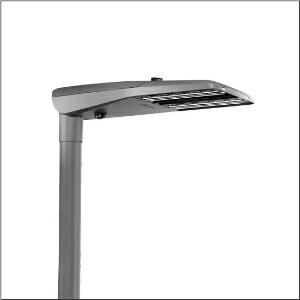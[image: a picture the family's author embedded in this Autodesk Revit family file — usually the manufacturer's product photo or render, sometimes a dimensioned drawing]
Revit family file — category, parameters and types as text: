
# Revit family: streetlight_sl_11_iq_midi___pc-r_5xc3f21y08me_3682
name_source: partatom
category: Lighting Fixtures
units: mm (PartAtom-declared; Revit-internal decimal feet)

## family parameters
Cut with Voids When Loaded = No
Host = Face
Light Source = No
Part Type = Normal
Room Calculation Point = No
Round Connector Dimension = Use Diameter
Shared = No

## types (1)
- --- (1 x LED, 12730 lm, 122.8 W, 2200K)
    Apparent Load = 123 VA
    CIE Flux Codes = 37 73 96 100 100
    Color Rendering = 70
    Color Temperature = 2200K
    Default Elevation = 1800 mm
    Description = Streetlight SL 11 iQ midi, mast luminaire, primary light control with 3 zone facetted reflector, of plastic, silver coated, highly specular, primary optical cover: cover, of PMMA, transparent, light distribution: PC-R, light emission: direct distribution, primary light characteristic: asymmetric, right, installation type: post-top, side-entry, LED, High Power LED, rated luminous flux: 12.730lm, luminous efficacy: 104lm/W, light colour: 722, colour temperature: 2200K, control: presetting dimming logarithmic, Street-Remote, Auto-Match, Temp-Guard, Lumen-Switch, Night-Set, Smart-Wire, Light-Fading, Desk-Remote (wireless, voltage-free reading and setting of iQ features in the workshop via application-optimized NFC function/RFID function), optimised constant luminous flux control (CLO 2.0), with cable H07RN-F 5x 1.5mm², mains connection: 230..240V, AC, 50/60Hz, connection cable pre-assembled, cable length: 12,5m, start of lifetime: 123W, end of service life: 130W, reduction: 56W, luminaire housing, of diecast aluminium, powder-coated, Siteco® metallic grey (DB 702S), please order mast flange separately, inclination adjustable without tools: 0°, 5°, 10°, 15° (post-top) | 0°, -5°, -10°, -15° (side-entry), sealing non-destructively replaceable, multi-level sealing system, length: 780mm, width: 376mm, height: 118mm, mast flange for spigot size: 42mm (side-entry): 5XC10008XM4, 60/48mm (side-entry/post-top): 5XC10108XM2, 76/60mm (side-entry/post-top): 5XC10108XM1, equipment: Power, Smart Interface below and above, protection rating (complete): IP66, insulation class (complete): insulation class II (safety insulation), certification: CE, ENEC, VDE, UKCA, impact resistance: IK09, permissible operating ambient temperature for outdoor applications: -25..+50°C, standard-compliant lighting for roads and squares, Environmental Product Declaration (EPD) tested and certified by an independent institute, packaging unit: 1 piece

Light Distribution: PC-R
    Height = 118 mm
    Lamp = 1 x LED
    Lamp Light Flux = 12730 lm
    Lamp Power = 122.8 W
    Lamp count = 1
    Length = 780 mm
    Luminous efficacy = 104 lm/W
    Manufacturer = Siteco
    ModVariant = No
    Model = 5XC3F21Y08ME
    Number of Poles = 1
    OnlyDefault = Yes
    Power Factor = 1
    Product Name = Streetlight SL 11 iQ midi | PC-R
    Product group = mast luminaire | pylon top
    ProductGroupID = 6100
    Protection Class = Protection class II
    Protection Degree = IP 66
    RLX_Detail_Level = 1
    RLX_Emergency_Light_Flux = 0 lm
    RLX_Emergency_Type = 0
    RLX_Emergency_Type_DB = No
    RlxData = <blob elided: 73473 chars, md5=d0c1b85f>
    Socket = socket
    Standby Power = 0 W
    System Light Flux = 12729 lm
    System Power = 123 W
    Type Comments = factory setting: luminous flux: 100 % | dim-lin: 254 | 553 mA
    Type Image = l_1004429.jpg
    URL = http://relux.com
    VarID = @adj_076267
    Voltage = 0 V
    Weight = 0.00 kg
    Width = 376 mm

## geometry (parser evidence)
native form markers: Blend x4, Sweep x11
no freeform markers — native parametric forms only
